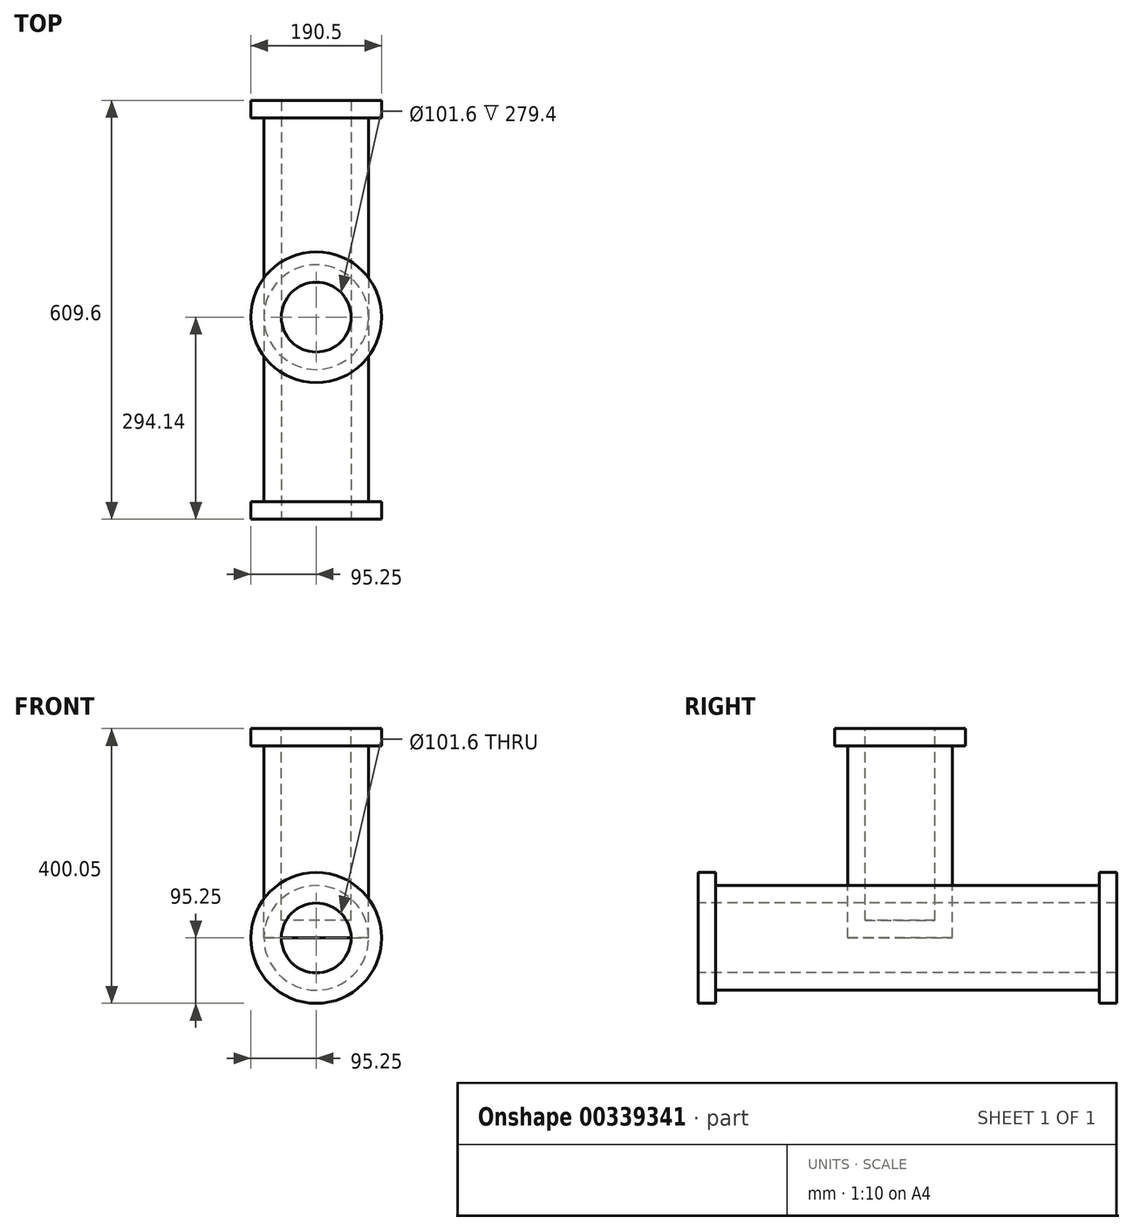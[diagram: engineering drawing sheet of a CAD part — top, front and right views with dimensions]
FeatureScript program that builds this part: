
annotation { "Feature Type Name" : "Feature", "Feature Type Description" : "" }
export const myFeature = defineFeature(function(context is Context, id is Id, definition is map)
    precondition{}
    {
        {
            var Q0;
            Q0=qCreatedBy(makeId("Right.planeOp"),FACE);
            var sketch = newSketch(context, id + "F0", { "sketchPlane" : qUnion([Q0])});
            skLineSegment(sketch, "E0", {"start": v(-294.14, 0) * mm, "end": v(315.46, 0) * mm});
            skLineSegment(sketch, "E1", {"start": v(0, 304.8) * mm, "end": v(0, 0) * mm});
            skSolve(sketch);
        }
        {
            var Q0;
            Q0=sQuery(id+"F0.wireOp",VERTEX,"E0.start");
            var Q1;
            Q1=qCreatedBy(makeId("Front.planeOp"),FACE);
            cPlane(context, id + "F1", {"entities" : qUnion([Q0, Q1]), "cplaneType" : CPlaneType.PLANE_POINT, "offset" : 320.04 * mm, "width" : 152.4 * mm, "height" : 152.4 * mm});
        }
        {
            var Q0;
            Q0=qCreatedBy(id+"F1.planeOp",FACE);
            var sketch = newSketch(context, id + "F2", { "sketchPlane" : qUnion([Q0])});
            skCircle(sketch, "E2", {"center": v(0, 0) * mm, "radius": 76.2 * mm});
            skSolve(sketch);
        }
        {
            var Q0;
            Q0=qCreatedBy(makeId("Top.planeOp"),FACE);
            var Q1;
            Q1=sQuery(id+"F0.wireOp",VERTEX,"E1.start");
            cPlane(context, id + "F3", {"entities" : qUnion([Q0, Q1]), "cplaneType" : CPlaneType.PLANE_POINT, "offset" : 25.4 * mm, "width" : 152.4 * mm, "height" : 152.4 * mm});
        }
        {
            var Q0;
            Q0=qCreatedBy(id+"F3.planeOp",FACE);
            var sketch = newSketch(context, id + "F4", { "sketchPlane" : qUnion([Q0])});
            skCircle(sketch, "E3", {"center": v(0, 0) * mm, "radius": 76.2 * mm});
            skSolve(sketch);
        }
        {
            var Q0;
            Q0=makeQuery(id+"F2.imprint","IMPRINT",FACE,{"disambiguationData":[TD([[makeQuery(id+"F2.imprint","IMPRINT",EDGE,{"derivedFrom":sQuery(id+"F2.wireOp",EDGE,"E2")}),1.0]])]});
            extrude(context, id + "F5", {"entities" : qUnion([Q0]), "oppositeDirection" : true, "depth" : 609.6 * mm});
        }
        {
            var Q0;
            Q0=makeQuery(id+"F4.imprint","IMPRINT",FACE,{"disambiguationData":[TD([[makeQuery(id+"F4.imprint","IMPRINT",EDGE,{"derivedFrom":sQuery(id+"F4.wireOp",EDGE,"E3")}),1.0]])]});
            extrude(context, id + "F6", {"entities" : qUnion([Q0]), "oppositeDirection" : true, "depth" : 304.8 * mm});
        }
        {
            var Q0;
            Q0=makeQuery(id+"F5.opExtrude","CAP_FACE",FACE,{"disambiguationData":[OSD([sQuery(id+"F2.wireOp",EDGE,"E2")])],"isStart":false});
            var Q1;
            Q1=makeQuery(id+"F6.opExtrude","CAP_FACE",FACE,{"disambiguationData":[OSD([sQuery(id+"F4.wireOp",EDGE,"E3")])],"isStart":true});
            var Q2;
            Q2=makeQuery(id+"F5.opExtrude","CAP_FACE",FACE,{"disambiguationData":[OSD([sQuery(id+"F2.wireOp",EDGE,"E2")])],"isStart":true});
            shell(context, id + "F7", {"entities" : qUnion([Q0, Q1, Q2]), "thickness" : 25.4 * mm});
        }
        {
            var Q0;
            Q0=sQuery(id+"F0.wireOp",EDGE,"E0");
            var Q1;
            Q1=sQuery(id+"F0.wireOp",VERTEX,"E0.start");
            cPlane(context, id + "F8", {"entities" : qUnion([Q0, Q1]), "cplaneType" : CPlaneType.LINE_POINT, "offset" : 25.4 * mm, "width" : 152.4 * mm, "height" : 152.4 * mm});
        }
        {
            var Q0;
            Q0=qCreatedBy(id+"F8.planeOp",FACE);
            var sketch = newSketch(context, id + "F9", { "sketchPlane" : qUnion([Q0])});
            skCircle(sketch, "E4", {"center": v(0, 0) * mm, "radius": 76.2 * mm});
            skCircle(sketch, "E5", {"center": v(0, 0) * mm, "radius": 95.25 * mm});
            skSolve(sketch);
        }
        {
            var Q0;
            Q0=makeQuery(id+"F9.imprint","IMPRINT",FACE,{"disambiguationData":[TD([[makeQuery(id+"F9.imprint","IMPRINT",EDGE,{"derivedFrom":sQuery(id+"F9.wireOp",EDGE,"E4")}),-1.0]])]});
            extrude(context, id + "F10", {"entities" : qUnion([Q0]), "operationType" : NewBodyOperationType.ADD, "depth" : 25.4 * mm, "offsetDistance" : 25.4 * mm});
        }
        {
            var Q0;
            Q0=sQuery(id+"F0.wireOp",EDGE,"E0");
            var Q1;
            Q1=sQuery(id+"F0.wireOp",VERTEX,"E0.end");
            cPlane(context, id + "F11", {"entities" : qUnion([Q0, Q1]), "cplaneType" : CPlaneType.LINE_POINT, "offset" : 25.4 * mm, "width" : 152.4 * mm, "height" : 152.4 * mm});
        }
        {
            var Q0;
            Q0=qCreatedBy(id+"F11.planeOp",FACE);
            var sketch = newSketch(context, id + "F12", { "sketchPlane" : qUnion([Q0])});
            skCircle(sketch, "E6", {"center": v(0, 0) * mm, "radius": 76.2 * mm});
            skCircle(sketch, "E7", {"center": v(0, 0) * mm, "radius": 95.25 * mm});
            skSolve(sketch);
        }
        {
            var Q0;
            Q0=makeQuery(id+"F12.imprint","IMPRINT",FACE,{"disambiguationData":[TD([[makeQuery(id+"F12.imprint","IMPRINT",EDGE,{"derivedFrom":sQuery(id+"F12.wireOp",EDGE,"E6")}),-1.0]])]});
            extrude(context, id + "F13", {"entities" : qUnion([Q0]), "operationType" : NewBodyOperationType.ADD, "depth" : -25.4 * mm, "offsetDistance" : 25.4 * mm});
        }
        {
            var Q0;
            Q0=qCreatedBy(id+"F3.planeOp",FACE);
            var sketch = newSketch(context, id + "F14", { "sketchPlane" : qUnion([Q0])});
            skCircle(sketch, "E8", {"center": v(0, 0) * mm, "radius": 76.2 * mm});
            skCircle(sketch, "E9", {"center": v(0, 0) * mm, "radius": 95.25 * mm});
            skSolve(sketch);
        }
        {
            var Q0;
            Q0=makeQuery(id+"F14.imprint","IMPRINT",FACE,{"disambiguationData":[TD([[makeQuery(id+"F14.imprint","IMPRINT",EDGE,{"derivedFrom":sQuery(id+"F14.wireOp",EDGE,"E8")}),-1.0]])]});
            extrude(context, id + "F15", {"entities" : qUnion([Q0]), "operationType" : NewBodyOperationType.ADD, "depth" : -25.4 * mm, "offsetDistance" : 25.4 * mm});
        }
    });
